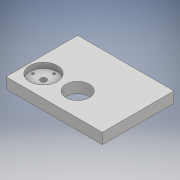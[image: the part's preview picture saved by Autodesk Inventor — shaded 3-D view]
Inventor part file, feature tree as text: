
AUTODESK INVENTOR PART (.ipt)
format: ipt  version: 2017 SP1 (Build 210196100, 196)  size: 137,728 bytes
history: native  units: mm
features: extrude x4, sketch x4
ambient origin geometry x8: Origin, YZ Plane, XZ Plane, XY Plane, X Axis, Y Axis, Z Axis, Center Point
bodies: Solide1 (feature_tree)
feature tree (8):
  extrude  "Extrusion1"  Depth=90.0mm
  extrude  "Extrusion2"  Depth=67.0mm
  extrude  "Extrusion3"  Depth=10.0mm TaperAngle=0.0deg
  extrude  "Extrusion4"  Depth=26.0mm
  sketch  "Esquisse1"
  sketch  "Esquisse2"
  sketch  "Esquisse3"
  sketch  "Esquisse4"
